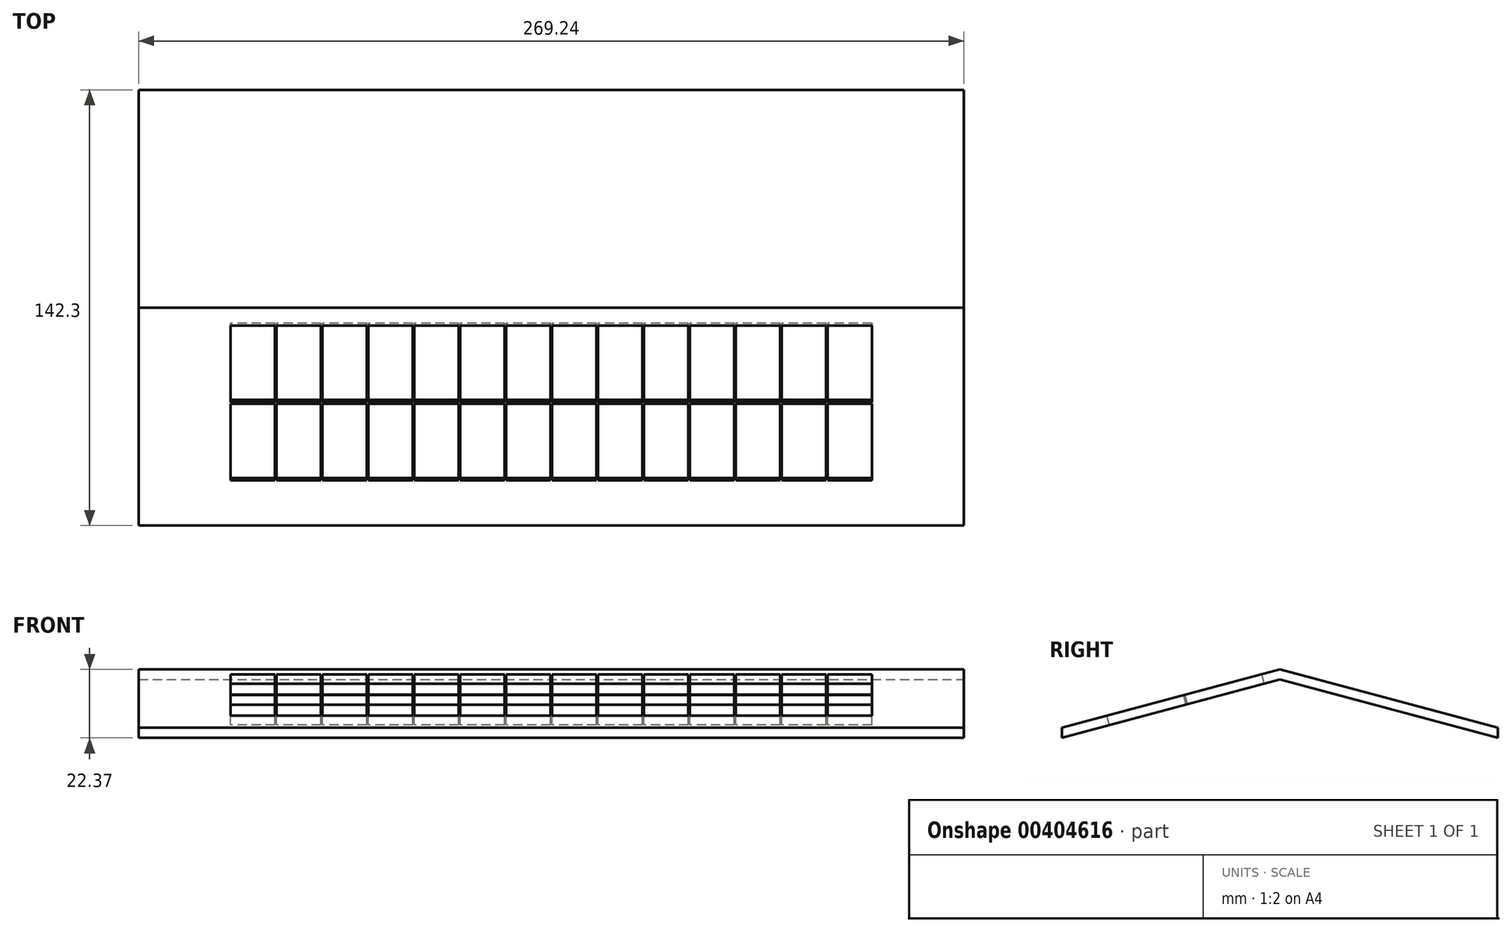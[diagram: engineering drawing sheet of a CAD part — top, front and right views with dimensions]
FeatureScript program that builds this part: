
annotation { "Feature Type Name" : "Feature", "Feature Type Description" : "" }
export const myFeature = defineFeature(function(context is Context, id is Id, definition is map)
    precondition{}
    {
        {
            var Q0;
            Q0=qCreatedBy(makeId("Right.planeOp"),FACE);
            var sketch = newSketch(context, id + "F0", { "sketchPlane" : qUnion([Q0])});
            skLineSegment(sketch, "E0", {"start": v(0, 0) * mm, "end": v(71.15, 19.06) * mm});
            skLineSegment(sketch, "E1", {"start": v(71.15, 19.06) * mm, "end": v(142.3, 0) * mm});
            skLineSegment(sketch, "E2", {"start": v(142.3, 0) * mm, "end": v(142.3, 3.3) * mm});
            skLineSegment(sketch, "E3", {"start": v(142.3, 3.3) * mm, "end": v(71.15, 22.37) * mm});
            skLineSegment(sketch, "E4", {"start": v(71.15, 22.37) * mm, "end": v(0, 3.3) * mm});
            skLineSegment(sketch, "E5", {"start": v(0, 3.3) * mm, "end": v(0, 0) * mm});
            skSolve(sketch);
        }
        {
            var Q0;
            Q0 = qSketchRegion(id + "F0", true);
            extrude(context, id + "F1", {"entities" : qUnion([Q0]), "oppositeDirection" : true, "depth" : 269.24 * mm});
        }
        {
            var Q0;
            Q0=makeQuery(id+"F1.opExtrude","SWEPT_FACE",FACE,{"disambiguationData":[OSD([sQuery(id+"F0.wireOp",EDGE,"E4")])]});
            var sketch = newSketch(context, id + "F2", { "sketchPlane" : qUnion([Q0])});
            skLineSegment(sketch, "E6.bottom", {"start": v(-239.27, 68.42) * mm, "end": v(-224.8, 68.42) * mm});
            skLineSegment(sketch, "E6.top", {"start": v(-239.27, 42.51) * mm, "end": v(-224.8, 42.51) * mm});
            skLineSegment(sketch, "E6.left", {"start": v(-239.27, 68.42) * mm, "end": v(-239.27, 42.51) * mm});
            skLineSegment(sketch, "E6.right", {"start": v(-224.8, 68.42) * mm, "end": v(-224.8, 42.51) * mm});
            skLineSegment(sketch, "E7.bottom", {"start": v(-239.27, 42) * mm, "end": v(-224.8, 42) * mm});
            skLineSegment(sketch, "E7.top", {"start": v(-239.27, 16.1) * mm, "end": v(-224.8, 16.1) * mm});
            skLineSegment(sketch, "E7.left", {"start": v(-239.27, 42) * mm, "end": v(-239.27, 16.1) * mm});
            skLineSegment(sketch, "E7.right", {"start": v(-224.8, 42) * mm, "end": v(-224.8, 16.1) * mm});
            skLineSegment(sketch, "E8.bottom", {"start": v(-224.28, 68.42) * mm, "end": v(-209.8, 68.42) * mm});
            skLineSegment(sketch, "E8.top", {"start": v(-224.28, 42.51) * mm, "end": v(-209.8, 42.51) * mm});
            skLineSegment(sketch, "E8.left", {"start": v(-224.28, 68.42) * mm, "end": v(-224.28, 42.51) * mm});
            skLineSegment(sketch, "E8.right", {"start": v(-209.8, 68.42) * mm, "end": v(-209.8, 42.51) * mm});
            skLineSegment(sketch, "E9.bottom", {"start": v(-224.28, 42) * mm, "end": v(-209.8, 42) * mm});
            skLineSegment(sketch, "E9.top", {"start": v(-224.28, 16.1) * mm, "end": v(-209.8, 16.1) * mm});
            skLineSegment(sketch, "E9.left", {"start": v(-224.28, 42) * mm, "end": v(-224.28, 16.1) * mm});
            skLineSegment(sketch, "E9.right", {"start": v(-209.8, 42) * mm, "end": v(-209.8, 16.1) * mm});
            skLineSegment(sketch, "E10.bottom", {"start": v(-209.3, 68.42) * mm, "end": v(-194.82, 68.42) * mm});
            skLineSegment(sketch, "E10.top", {"start": v(-209.3, 42.51) * mm, "end": v(-194.82, 42.51) * mm});
            skLineSegment(sketch, "E10.left", {"start": v(-209.3, 68.42) * mm, "end": v(-209.3, 42.51) * mm});
            skLineSegment(sketch, "E10.right", {"start": v(-194.82, 68.42) * mm, "end": v(-194.82, 42.51) * mm});
            skLineSegment(sketch, "E11.bottom", {"start": v(-209.3, 42) * mm, "end": v(-194.82, 42) * mm});
            skLineSegment(sketch, "E11.top", {"start": v(-209.3, 16.1) * mm, "end": v(-194.82, 16.1) * mm});
            skLineSegment(sketch, "E11.left", {"start": v(-209.3, 42) * mm, "end": v(-209.3, 16.1) * mm});
            skLineSegment(sketch, "E11.right", {"start": v(-194.82, 42) * mm, "end": v(-194.82, 16.1) * mm});
            skLineSegment(sketch, "E12.bottom", {"start": v(-194.31, 68.42) * mm, "end": v(-179.83, 68.42) * mm});
            skLineSegment(sketch, "E12.top", {"start": v(-194.31, 42.51) * mm, "end": v(-179.83, 42.51) * mm});
            skLineSegment(sketch, "E12.left", {"start": v(-194.31, 68.42) * mm, "end": v(-194.31, 42.51) * mm});
            skLineSegment(sketch, "E12.right", {"start": v(-179.83, 68.42) * mm, "end": v(-179.83, 42.51) * mm});
            skLineSegment(sketch, "E13.bottom", {"start": v(-194.31, 42) * mm, "end": v(-179.83, 42) * mm});
            skLineSegment(sketch, "E13.top", {"start": v(-194.31, 16.1) * mm, "end": v(-179.83, 16.1) * mm});
            skLineSegment(sketch, "E13.left", {"start": v(-194.31, 42) * mm, "end": v(-194.31, 16.1) * mm});
            skLineSegment(sketch, "E13.right", {"start": v(-179.83, 42) * mm, "end": v(-179.83, 16.1) * mm});
            skLineSegment(sketch, "E14.bottom", {"start": v(-179.32, 68.42) * mm, "end": v(-164.85, 68.42) * mm});
            skLineSegment(sketch, "E14.top", {"start": v(-179.32, 42.51) * mm, "end": v(-164.85, 42.51) * mm});
            skLineSegment(sketch, "E14.left", {"start": v(-179.32, 68.42) * mm, "end": v(-179.32, 42.51) * mm});
            skLineSegment(sketch, "E14.right", {"start": v(-164.85, 68.42) * mm, "end": v(-164.85, 42.51) * mm});
            skLineSegment(sketch, "E15.bottom", {"start": v(-179.32, 42) * mm, "end": v(-164.85, 42) * mm});
            skLineSegment(sketch, "E15.top", {"start": v(-179.32, 16.1) * mm, "end": v(-164.85, 16.1) * mm});
            skLineSegment(sketch, "E15.left", {"start": v(-179.32, 42) * mm, "end": v(-179.32, 16.1) * mm});
            skLineSegment(sketch, "E15.right", {"start": v(-164.85, 42) * mm, "end": v(-164.85, 16.1) * mm});
            skLineSegment(sketch, "E16.bottom", {"start": v(-164.34, 68.42) * mm, "end": v(-149.86, 68.42) * mm});
            skLineSegment(sketch, "E16.top", {"start": v(-164.34, 42.51) * mm, "end": v(-149.86, 42.51) * mm});
            skLineSegment(sketch, "E16.left", {"start": v(-164.34, 68.42) * mm, "end": v(-164.34, 42.51) * mm});
            skLineSegment(sketch, "E16.right", {"start": v(-149.86, 68.42) * mm, "end": v(-149.86, 42.51) * mm});
            skLineSegment(sketch, "E17.bottom", {"start": v(-164.34, 42) * mm, "end": v(-149.86, 42) * mm});
            skLineSegment(sketch, "E17.top", {"start": v(-164.34, 16.1) * mm, "end": v(-149.86, 16.1) * mm});
            skLineSegment(sketch, "E17.left", {"start": v(-164.34, 42) * mm, "end": v(-164.34, 16.1) * mm});
            skLineSegment(sketch, "E17.right", {"start": v(-149.86, 42) * mm, "end": v(-149.86, 16.1) * mm});
            skLineSegment(sketch, "E18.bottom", {"start": v(-149.35, 68.42) * mm, "end": v(-134.87, 68.42) * mm});
            skLineSegment(sketch, "E18.top", {"start": v(-149.35, 42.51) * mm, "end": v(-134.87, 42.51) * mm});
            skLineSegment(sketch, "E18.left", {"start": v(-149.35, 68.42) * mm, "end": v(-149.35, 42.51) * mm});
            skLineSegment(sketch, "E18.right", {"start": v(-134.87, 68.42) * mm, "end": v(-134.87, 42.51) * mm});
            skLineSegment(sketch, "E19.bottom", {"start": v(-149.35, 42) * mm, "end": v(-134.87, 42) * mm});
            skLineSegment(sketch, "E19.top", {"start": v(-149.35, 16.1) * mm, "end": v(-134.87, 16.1) * mm});
            skLineSegment(sketch, "E19.left", {"start": v(-149.35, 42) * mm, "end": v(-149.35, 16.1) * mm});
            skLineSegment(sketch, "E19.right", {"start": v(-134.87, 42) * mm, "end": v(-134.87, 16.1) * mm});
            skLineSegment(sketch, "E20.bottom", {"start": v(-134.37, 68.42) * mm, "end": v(-119.89, 68.42) * mm});
            skLineSegment(sketch, "E20.top", {"start": v(-134.37, 42.51) * mm, "end": v(-119.89, 42.51) * mm});
            skLineSegment(sketch, "E20.left", {"start": v(-134.37, 68.42) * mm, "end": v(-134.37, 42.51) * mm});
            skLineSegment(sketch, "E20.right", {"start": v(-119.89, 68.42) * mm, "end": v(-119.89, 42.51) * mm});
            skLineSegment(sketch, "E21.bottom", {"start": v(-134.37, 42) * mm, "end": v(-119.89, 42) * mm});
            skLineSegment(sketch, "E21.top", {"start": v(-134.37, 16.1) * mm, "end": v(-119.89, 16.1) * mm});
            skLineSegment(sketch, "E21.left", {"start": v(-134.37, 42) * mm, "end": v(-134.37, 16.1) * mm});
            skLineSegment(sketch, "E21.right", {"start": v(-119.89, 42) * mm, "end": v(-119.89, 16.1) * mm});
            skLineSegment(sketch, "E22.bottom", {"start": v(-119.38, 68.42) * mm, "end": v(-104.9, 68.42) * mm});
            skLineSegment(sketch, "E22.top", {"start": v(-119.38, 42.51) * mm, "end": v(-104.9, 42.51) * mm});
            skLineSegment(sketch, "E22.left", {"start": v(-119.38, 68.42) * mm, "end": v(-119.38, 42.51) * mm});
            skLineSegment(sketch, "E22.right", {"start": v(-104.9, 68.42) * mm, "end": v(-104.9, 42.51) * mm});
            skLineSegment(sketch, "E23.bottom", {"start": v(-119.38, 42) * mm, "end": v(-104.9, 42) * mm});
            skLineSegment(sketch, "E23.top", {"start": v(-119.38, 16.1) * mm, "end": v(-104.9, 16.1) * mm});
            skLineSegment(sketch, "E23.left", {"start": v(-119.38, 42) * mm, "end": v(-119.38, 16.1) * mm});
            skLineSegment(sketch, "E23.right", {"start": v(-104.9, 42) * mm, "end": v(-104.9, 16.1) * mm});
            skLineSegment(sketch, "E24.bottom", {"start": v(-104.4, 68.42) * mm, "end": v(-89.92, 68.42) * mm});
            skLineSegment(sketch, "E24.top", {"start": v(-104.4, 42.51) * mm, "end": v(-89.92, 42.51) * mm});
            skLineSegment(sketch, "E24.left", {"start": v(-104.4, 68.42) * mm, "end": v(-104.4, 42.51) * mm});
            skLineSegment(sketch, "E24.right", {"start": v(-89.92, 68.42) * mm, "end": v(-89.92, 42.51) * mm});
            skLineSegment(sketch, "E25.bottom", {"start": v(-104.4, 42) * mm, "end": v(-89.92, 42) * mm});
            skLineSegment(sketch, "E25.top", {"start": v(-104.4, 16.1) * mm, "end": v(-89.92, 16.1) * mm});
            skLineSegment(sketch, "E25.left", {"start": v(-104.4, 42) * mm, "end": v(-104.4, 16.1) * mm});
            skLineSegment(sketch, "E25.right", {"start": v(-89.92, 42) * mm, "end": v(-89.92, 16.1) * mm});
            skLineSegment(sketch, "E26.bottom", {"start": v(-89.4, 68.42) * mm, "end": v(-74.93, 68.42) * mm});
            skLineSegment(sketch, "E26.top", {"start": v(-89.4, 42.51) * mm, "end": v(-74.93, 42.51) * mm});
            skLineSegment(sketch, "E26.left", {"start": v(-89.4, 68.42) * mm, "end": v(-89.4, 42.51) * mm});
            skLineSegment(sketch, "E26.right", {"start": v(-74.93, 68.42) * mm, "end": v(-74.93, 42.51) * mm});
            skLineSegment(sketch, "E27.bottom", {"start": v(-89.4, 42) * mm, "end": v(-74.93, 42) * mm});
            skLineSegment(sketch, "E27.top", {"start": v(-89.4, 16.1) * mm, "end": v(-74.93, 16.1) * mm});
            skLineSegment(sketch, "E27.left", {"start": v(-89.4, 42) * mm, "end": v(-89.4, 16.1) * mm});
            skLineSegment(sketch, "E27.right", {"start": v(-74.93, 42) * mm, "end": v(-74.93, 16.1) * mm});
            skLineSegment(sketch, "E28.bottom", {"start": v(-74.42, 68.42) * mm, "end": v(-59.94, 68.42) * mm});
            skLineSegment(sketch, "E28.top", {"start": v(-74.42, 42.51) * mm, "end": v(-59.94, 42.51) * mm});
            skLineSegment(sketch, "E28.left", {"start": v(-74.42, 68.42) * mm, "end": v(-74.42, 42.51) * mm});
            skLineSegment(sketch, "E28.right", {"start": v(-59.94, 68.42) * mm, "end": v(-59.94, 42.51) * mm});
            skLineSegment(sketch, "E29.bottom", {"start": v(-74.42, 42) * mm, "end": v(-59.94, 42) * mm});
            skLineSegment(sketch, "E29.top", {"start": v(-74.42, 16.1) * mm, "end": v(-59.94, 16.1) * mm});
            skLineSegment(sketch, "E29.left", {"start": v(-74.42, 42) * mm, "end": v(-74.42, 16.1) * mm});
            skLineSegment(sketch, "E29.right", {"start": v(-59.94, 42) * mm, "end": v(-59.94, 16.1) * mm});
            skLineSegment(sketch, "E30.bottom", {"start": v(-59.44, 68.42) * mm, "end": v(-44.96, 68.42) * mm});
            skLineSegment(sketch, "E30.top", {"start": v(-59.44, 42.51) * mm, "end": v(-44.96, 42.51) * mm});
            skLineSegment(sketch, "E30.left", {"start": v(-59.44, 68.42) * mm, "end": v(-59.44, 42.51) * mm});
            skLineSegment(sketch, "E30.right", {"start": v(-44.96, 68.42) * mm, "end": v(-44.96, 42.51) * mm});
            skLineSegment(sketch, "E31.bottom", {"start": v(-59.44, 42) * mm, "end": v(-44.96, 42) * mm});
            skLineSegment(sketch, "E31.top", {"start": v(-59.44, 16.1) * mm, "end": v(-44.96, 16.1) * mm});
            skLineSegment(sketch, "E31.left", {"start": v(-59.44, 42) * mm, "end": v(-59.44, 16.1) * mm});
            skLineSegment(sketch, "E31.right", {"start": v(-44.96, 42) * mm, "end": v(-44.96, 16.1) * mm});
            skLineSegment(sketch, "E32.bottom", {"start": v(-44.45, 68.42) * mm, "end": v(-29.97, 68.42) * mm});
            skLineSegment(sketch, "E32.top", {"start": v(-44.45, 42.51) * mm, "end": v(-29.97, 42.51) * mm});
            skLineSegment(sketch, "E32.left", {"start": v(-44.45, 68.42) * mm, "end": v(-44.45, 42.51) * mm});
            skLineSegment(sketch, "E32.right", {"start": v(-29.97, 68.42) * mm, "end": v(-29.97, 42.51) * mm});
            skLineSegment(sketch, "E33.bottom", {"start": v(-44.45, 42) * mm, "end": v(-29.97, 42) * mm});
            skLineSegment(sketch, "E33.top", {"start": v(-44.45, 16.1) * mm, "end": v(-29.97, 16.1) * mm});
            skLineSegment(sketch, "E33.left", {"start": v(-44.45, 42) * mm, "end": v(-44.45, 16.1) * mm});
            skLineSegment(sketch, "E33.right", {"start": v(-29.97, 42) * mm, "end": v(-29.97, 16.1) * mm});
            skSolve(sketch);
        }
        {
            var Q0;
            Q0 = qSketchRegion(id + "F2", true);
            extrude(context, id + "F3", {"entities" : qUnion([Q0]), "operationType" : NewBodyOperationType.REMOVE, "oppositeDirection" : true, "depth" : 25.4 * mm});
        }
    });
